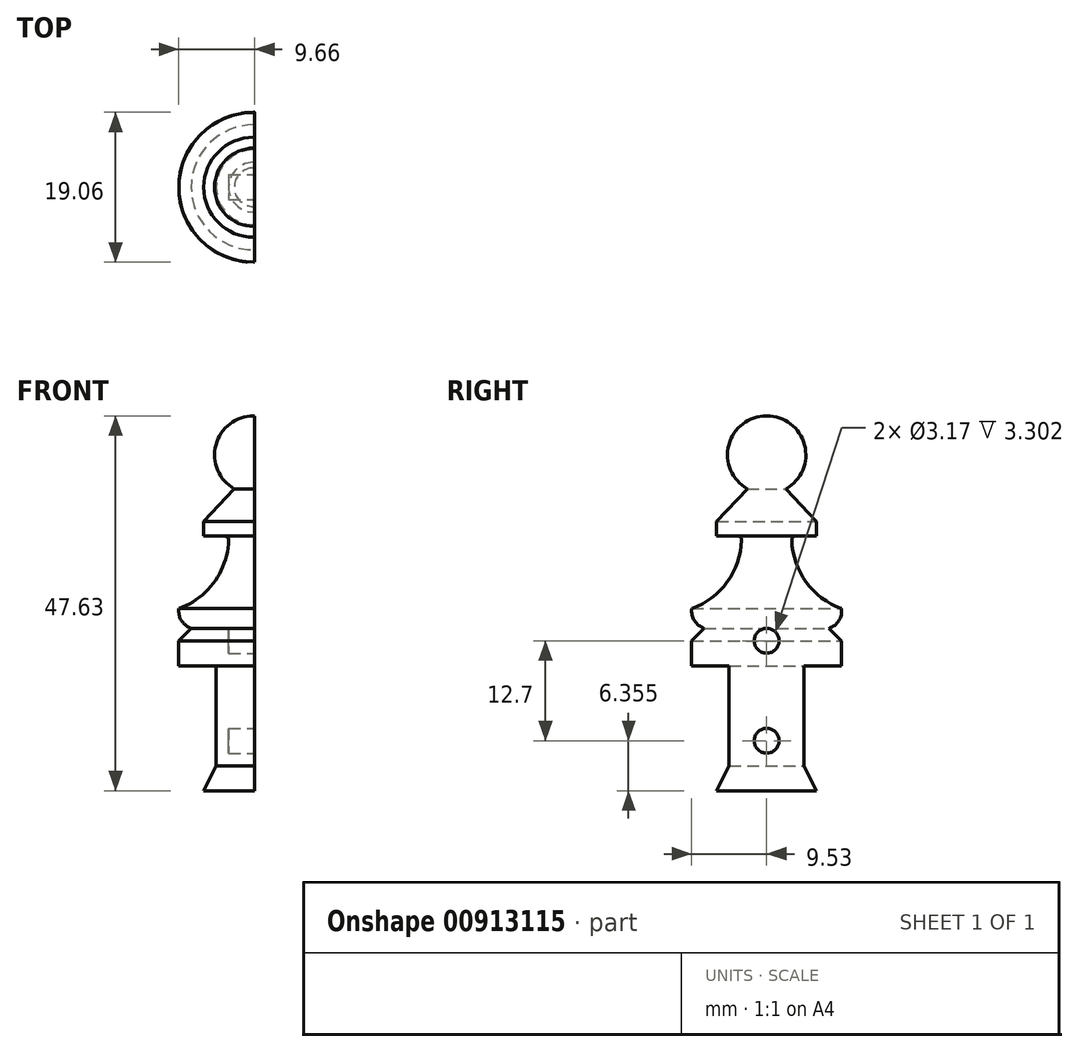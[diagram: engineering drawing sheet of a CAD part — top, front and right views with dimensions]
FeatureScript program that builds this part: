
annotation { "Feature Type Name" : "Feature", "Feature Type Description" : "" }
export const myFeature = defineFeature(function(context is Context, id is Id, definition is map)
    precondition{}
    {
        {
            var Q0;
            Q0=qCreatedBy(makeId("Right.planeOp"),FACE);
            var sketch = newSketch(context, id + "F0", { "sketchPlane" : qUnion([Q0])});
            skLineSegment(sketch, "E0", {"start": v(0, 0) * mm, "end": v(0, 31.75) * mm});
            skLineSegment(sketch, "E1", {"start": v(0, 0) * mm, "end": v(9.53, 0) * mm});
            skLineSegment(sketch, "E2", {"start": v(9.53, 0) * mm, "end": v(9.53, 3.18) * mm});
            skLineSegment(sketch, "E3", {"start": v(9.53, 3.17) * mm, "end": v(7.94, 4.76) * mm});
            skArc(sketch, "E4", {"start": v(7.94, 4.76) * mm, "mid": v(9.17, 5.73) * mm, "end": v(9.5, 7.25) * mm});
            skArc(sketch, "E5", {"start": v(3.18, 16.47) * mm, "mid": v(4.87, 10.85) * mm, "end": v(9.5, 7.25) * mm});
            skLineSegment(sketch, "E6", {"start": v(3.18, 16.47) * mm, "end": v(6.35, 16.47) * mm});
            skLineSegment(sketch, "E7", {"start": v(6.35, 16.47) * mm, "end": v(6.35, 18.32) * mm});
            skLineSegment(sketch, "E8", {"start": v(6.35, 18.32) * mm, "end": v(2.47, 22.46) * mm});
            skArc(sketch, "E9", {"start": v(2.47, 22.46) * mm, "mid": v(4.8, 28.05) * mm, "end": v(0, 31.75) * mm});
            skLineSegment(sketch, "E10.bottom", {"start": v(0, 0) * mm, "end": v(4.76, 0) * mm});
            skLineSegment(sketch, "E10.top", {"start": v(0, -12.7) * mm, "end": v(4.76, -12.7) * mm});
            skLineSegment(sketch, "E10.left", {"start": v(0, 0) * mm, "end": v(0, -12.7) * mm});
            skLineSegment(sketch, "E10.right", {"start": v(4.76, 0) * mm, "end": v(4.76, -12.7) * mm});
            skLineSegment(sketch, "E11", {"start": v(4.76, -12.7) * mm, "end": v(6.35, -15.88) * mm});
            skLineSegment(sketch, "E12", {"start": v(6.35, -15.87) * mm, "end": v(0, -15.87) * mm});
            skLineSegment(sketch, "E13", {"start": v(0, -15.87) * mm, "end": v(0, -12.7) * mm});
            skSolve(sketch);
        }
        {
            var Q0;
            {var subQ0=sQuery(id+"F0.wireOp",EDGE,"E0");Q0=makeQuery(id+"F0.imprint","IMPRINT",FACE,{"disambiguationData":[TD([[makeQuery(id+"F0.imprint","IMPRINT",EDGE,{"derivedFrom":subQ0}),-1.0]])]});}
            var Q1;
            Q1=makeQuery(id+"F0.imprint","IMPRINT",FACE,{"disambiguationData":[TD([[makeQuery(id+"F0.imprint","IMPRINT",EDGE,{"derivedFrom":sQuery(id+"F0.wireOp",EDGE,"E10.top")}),1.0]])]});
            var Q2;
            Q2=makeQuery(id+"F0.imprint","IMPRINT",FACE,{"disambiguationData":[TD([[makeQuery(id+"F0.imprint","IMPRINT",EDGE,{"derivedFrom":sQuery(id+"F0.wireOp",EDGE,"E10.top")}),-1.0]])]});
            var Q3;
            Q3=sQuery(id+"F0.wireOp",EDGE,"E0");
            revolve(context, id + "F1", {"entities" : qUnion([Q0, Q1, Q2]), "axis" : qUnion([Q3]), "revolveType" : RevolveType.ONE_DIRECTION, "angle" : 180 * degree, "surfaceOperationType" : NewSurfaceOperationType.NEW});
        }
        {
            var Q0;
            Q0=makeQuery(id+"F1.opRevolve","CAP_FACE",FACE,{"disambiguationData":[OSD([sQuery(id+"F0.wireOp",EDGE,"E0"),sQuery(id+"F0.wireOp",EDGE,"E1"),sQuery(id+"F0.wireOp",EDGE,"E2"),sQuery(id+"F0.wireOp",EDGE,"E3"),sQuery(id+"F0.wireOp",EDGE,"E4"),sQuery(id+"F0.wireOp",EDGE,"E5"),sQuery(id+"F0.wireOp",EDGE,"E6"),sQuery(id+"F0.wireOp",EDGE,"E7"),sQuery(id+"F0.wireOp",EDGE,"E8"),sQuery(id+"F0.wireOp",EDGE,"E9"),sQuery(id+"F0.wireOp",EDGE,"E10.left"),sQuery(id+"F0.wireOp",EDGE,"E10.right"),sQuery(id+"F0.wireOp",EDGE,"E11"),sQuery(id+"F0.wireOp",EDGE,"E12"),sQuery(id+"F0.wireOp",EDGE,"E13")])],"isStart":false});
            var sketch = newSketch(context, id + "F2", { "sketchPlane" : qUnion([Q0])});
            skCircle(sketch, "E14", {"center": v(0, 3.18) * mm, "radius": 1.59 * mm});
            skCircle(sketch, "E15", {"center": v(0, -9.52) * mm, "radius": 1.59 * mm});
            skSolve(sketch);
        }
        {
            var Q0;
            Q0=makeQuery(id+"F2.imprint","IMPRINT",FACE,{"disambiguationData":[TD([[makeQuery(id+"F2.imprint","IMPRINT",EDGE,{"derivedFrom":sQuery(id+"F2.wireOp",EDGE,"E14")}),1.0]])]});
            var Q1;
            Q1=makeQuery(id+"F2.imprint","IMPRINT",FACE,{"disambiguationData":[TD([[makeQuery(id+"F2.imprint","IMPRINT",EDGE,{"derivedFrom":sQuery(id+"F2.wireOp",EDGE,"E15")}),1.0]])]});
            extrude(context, id + "F3", {"entities" : qUnion([Q0, Q1]), "operationType" : NewBodyOperationType.REMOVE, "oppositeDirection" : true, "depth" : 3.17 * mm, "offsetDistance" : 25.4 * mm});
        }
        {
            var Q0;
            Q0=makeQuery(id+"F1.opRevolve","SWEPT_EDGE",EDGE,{"disambiguationData":[OSD([sQuery(id+"F0.wireOp",EDGE,"E5"),sQuery(id+"F0.wireOp",EDGE,"E6")])]});
            fillet(context, id + "F4", {"entities" : qUnion([Q0]), "radius" : 0.5 * mm, "tangentPropagation" : true, "allowEdgeOverflow" : false});
        }
        {
            var Q0;
            Q0=makeQuery(id+"F1.opRevolve","CAP_FACE",FACE,{"disambiguationData":[OSD([sQuery(id+"F0.wireOp",EDGE,"E0"),sQuery(id+"F0.wireOp",EDGE,"E1"),sQuery(id+"F0.wireOp",EDGE,"E2"),sQuery(id+"F0.wireOp",EDGE,"E3"),sQuery(id+"F0.wireOp",EDGE,"E4"),sQuery(id+"F0.wireOp",EDGE,"E5"),sQuery(id+"F0.wireOp",EDGE,"E6"),sQuery(id+"F0.wireOp",EDGE,"E7"),sQuery(id+"F0.wireOp",EDGE,"E8"),sQuery(id+"F0.wireOp",EDGE,"E9"),sQuery(id+"F0.wireOp",EDGE,"E10.left"),sQuery(id+"F0.wireOp",EDGE,"E10.right"),sQuery(id+"F0.wireOp",EDGE,"E11"),sQuery(id+"F0.wireOp",EDGE,"E12"),sQuery(id+"F0.wireOp",EDGE,"E13")])],"isStart":false});
            extrude(context, id + "F5", {"entities" : qUnion([Q0]), "operationType" : NewBodyOperationType.ADD, "depth" : 0.13 * mm, "offsetDistance" : 25.4 * mm});
        }
    });
